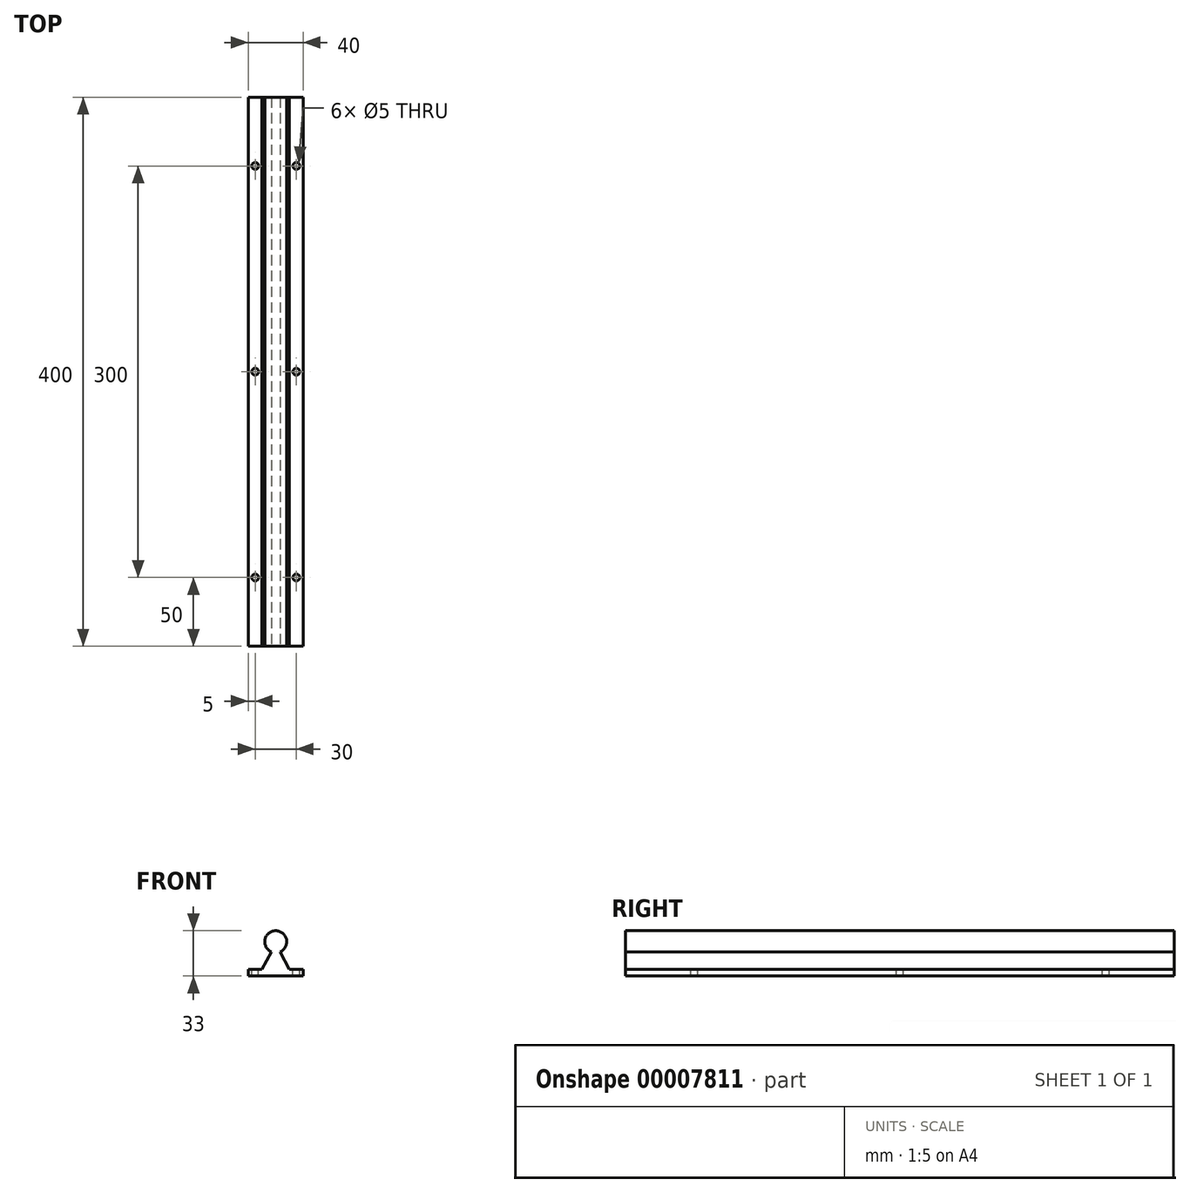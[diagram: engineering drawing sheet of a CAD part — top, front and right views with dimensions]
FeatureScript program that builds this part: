
annotation { "Feature Type Name" : "Feature", "Feature Type Description" : "" }
export const myFeature = defineFeature(function(context is Context, id is Id, definition is map)
    precondition{}
    {
        {
            var Q0;
            Q0=qCreatedBy(makeId("Front.planeOp"),FACE);
            var sketch = newSketch(context, id + "F0", { "sketchPlane" : qUnion([Q0])});
            skLineSegment(sketch, "E0", {"start": v(-20, 0) * mm, "end": v(20, 0) * mm});
            skLineSegment(sketch, "E1.top", {"start": v(-20, 5) * mm, "end": v(-10, 5) * mm});
            skLineSegment(sketch, "E1.left", {"start": v(-20, 0) * mm, "end": v(-20, 5) * mm});
            skLineSegment(sketch, "E1.right", {"start": v(20, 0) * mm, "end": v(20, 5) * mm});
            skPoint(sketch, "E2", {"position": v(0, 25) * mm});
            skArc(sketch, "E3", {"start": v(3.21, 17.67) * mm, "mid": v(0, 33) * mm, "end": v(-3.21, 17.67) * mm});
            skLineSegment(sketch, "E4", {"start": v(-3.21, 17.67) * mm, "end": v(-10, 5) * mm});
            skLineSegment(sketch, "E5", {"start": v(10, 5) * mm, "end": v(3.21, 17.67) * mm});
            skLineSegment(sketch, "E6.trimOffspring", {"start": v(10, 5) * mm, "end": v(20, 5) * mm});
            skSolve(sketch);
        }
        {
            var Q0;
            Q0 = qSketchRegion(id + "F0", true);
            extrude(context, id + "F1", {"entities" : qUnion([Q0]), "oppositeDirection" : true, "depth" : 400 * mm});
        }
        {
            var Q0;
            Q0=makeQuery(id+"F1.opExtrude","SWEPT_FACE",FACE,{"disambiguationData":[OSD([sQuery(id+"F0.wireOp",EDGE,"E6.trimOffspring")])]});
            var sketch = newSketch(context, id + "F2", { "sketchPlane" : qUnion([Q0])});
            skLineSegment(sketch, "E7.0", {"start": v(15, 400) * mm, "end": v(15, 0) * mm});
            skLineSegment(sketch, "E8.0", {"start": v(-15, 400) * mm, "end": v(-15, 0) * mm});
            skLineSegment(sketch, "E9.0", {"start": v(10, 50) * mm, "end": v(20, 50) * mm});
            skLineSegment(sketch, "E10.0", {"start": v(10, 200) * mm, "end": v(20, 200) * mm});
            skLineSegment(sketch, "E11.0", {"start": v(10, 350) * mm, "end": v(20, 350) * mm});
            skLineSegment(sketch, "E12.0", {"start": v(-20, 350) * mm, "end": v(-10, 350) * mm});
            skLineSegment(sketch, "E13.0", {"start": v(-20, 200) * mm, "end": v(-10, 200) * mm});
            skLineSegment(sketch, "E14.0", {"start": v(-20, 50) * mm, "end": v(-10, 50) * mm});
            skCircle(sketch, "E15", {"center": v(-15, 50) * mm, "radius": 2.5 * mm});
            skCircle(sketch, "E16", {"center": v(15, 50) * mm, "radius": 2.5 * mm});
            skCircle(sketch, "E17", {"center": v(-15, 200) * mm, "radius": 2.5 * mm});
            skCircle(sketch, "E18", {"center": v(15, 200) * mm, "radius": 2.5 * mm});
            skCircle(sketch, "E19", {"center": v(15, 350) * mm, "radius": 2.5 * mm});
            skCircle(sketch, "E20", {"center": v(-15, 350) * mm, "radius": 2.5 * mm});
            skSolve(sketch);
        }
        {
            var Q0;
            Q0 = qSketchRegion(id + "F2", true);
            extrude(context, id + "F3", {"entities" : qUnion([Q0]), "operationType" : NewBodyOperationType.REMOVE, "oppositeDirection" : true, "depth" : 25 * mm});
        }
    });
